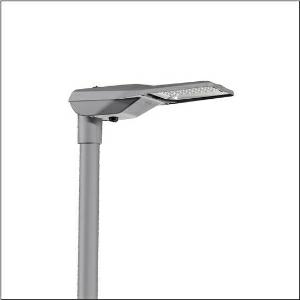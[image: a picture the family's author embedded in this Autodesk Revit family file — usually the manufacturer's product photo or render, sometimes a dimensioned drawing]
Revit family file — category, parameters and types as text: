
# Revit family: streetlight_sl_21_mini___pl52_5xe2h33t08hb_6eb8
name_source: partatom
category: Lighting Fixtures
units: mm (PartAtom-declared; Revit-internal decimal feet)

## family parameters
Cut with Voids When Loaded = No
Host = Face
Light Source = No
Part Type = Normal
Room Calculation Point = No
Round Connector Dimension = Use Diameter
Shared = No

## types (1)
- --- (1 x LED, 8890 lm, 66 W, 3000K)
    Apparent Load = 66 VA
    CIE Flux Codes = 27 59 98 100 100
    Color Rendering = 70
    Color Temperature = 3000K
    Default Elevation = 1800 mm
    Description = Streetlight SL 21 mini, mast luminaire, primary light control with lens, of PMMA, primary optical cover: cover, of toughened safety glass, transparent, light distribution: PL52, light emission: direct distribution, primary light characteristic: asymmetric, installation type: side-entry, post-top, LED, High Power LED, rated luminous flux: 8.890lm, luminous efficacy: 135lm/W, light colour: 730, colour temperature: 3000K, control gear: D4i, control: overheat protection, constant luminous flux control, time-dependent luminous flux control, flexible luminous flux parameterisation, pre-setting: logarithmic dimming characteristic, mains connection: 220..240V, AC, 50/60Hz, start of lifetime: 66W, end of service life: 69W, reduction: 30W, luminaire housing, of diecast aluminium, powder-coated, Siteco® metallic grey (DB 702S), corrosivity category C5 mid according to DIN EN ISO 12944, please order mast flange separately, inclination adjustable: 0°, 5°, 10°, 15°, sealing non-destructively replaceable, multi-level sealing system, length: 628mm, width: 235mm, height: 110mm, mast flange for spigot size: 42mm (side-entry): 5XC10008XM4, 60/48mm (side-entry/post-top): 5XC10108XM2, 76/60mm (side-entry/post-top): 5XC10108XM1, mounting height: 4..8m, Smart Interface below and above, protection rating (complete): IP66, insulation class (complete): insulation class II (safety insulation), certification: CE, ENEC, ENEC+, VDE, impact resistance: IK10, permissible operating ambient temperature for outdoor applications: -40..+50°C, standard-compliant lighting for roads and squares, packaging unit: 1 piece

Light Distribution: PL52
    Height = 110 mm
    Lamp = 1 x LED
    Lamp Light Flux = 8890 lm
    Lamp Power = 66 W
    Lamp count = 1
    Length = 625 mm
    Luminous efficacy = 135 lm/W
    Manufacturer = Siteco
    ModVariant = No
    Model = 5XE2H33T08HB
    Number of Poles = 1
    OnlyDefault = Yes
    Power Factor = 1
    Product Name = Streetlight SL 21 mini | PL52
    Product group = mast luminaire | pylon top
    ProductGroupID = 6100
    Protection Class = Protection class II
    Protection Degree = IP 66
    RLX_Detail_Level = 1
    RLX_Emergency_Light_Flux = 0 lm
    RLX_Emergency_Type = 0
    RLX_Emergency_Type_DB = No
    RlxData = <blob elided: 35853 chars, md5=11e9ffa8>
    Socket = socket
    Standby Power = 0 W
    System Light Flux = 8890 lm
    System Power = 66 W
    Type Comments = factory setting: luminous flux: 100 % | dim-lin: 254 | 670 mA
    Type Image = l_1003514.jpg
    URL = http://relux.com
    VarID = @adj_189982
    Voltage = 0 V
    Weight = 0.00 kg
    Width = 234 mm

## geometry (parser evidence)
native form markers: Blend x4, Sweep x9
no freeform markers — native parametric forms only
